# Revit family: Genelec_4410
name_source: partatom
category: Generic Models
units: mm (PartAtom-declared; Revit-internal decimal feet)

## family parameters
Always vertical = No
Can host rebar = No
Cut with Voids When Loaded = No
Maintain Annotation Orientation = No
Part Type = Normal
Room Calculation Point = Yes
Round Connector Dimension = Use Diameter
Shared = No
Work Plane-Based = No

## types (2) — shared parameters
Accuracy of Frequency Response = ± 2.5 dB (74 Hz - 20 kHz)
Acoustic Axis = 107
BIMobject category = Audio Electronics
Color = RAL_9018_Papyrus White
Connections = 1 x RJ45 for PoE power, management and audio in AES67 / Dante format
Default Elevation = 1200 mm
Depth = 115 mm  [stored 0.377297 ft]
Description = The most compact in the Smart IP family, the 4410A Active PoE-Powered Installation Loudspeaker produces uncompromised SPL and acoustic performance.
Dispersion Angle = H 130° V 110°
Driver Dimensions = ⌀ 76 mm Woofer+ ⌀ 19 mm Tweeter
Export Type to IFC As = IfcAudioVisualApplianceType
Finish Type = Die cast aluminium
Frequency Response = 67 Hz - 40 kHz (-6 dB)
Height = 181 mm  [stored 0.593832 ft]
IFC Classification = Electric Appliance
IFC Name = 4410A
Line Drawing = https://assets.ctfassets.net
Mains Voltage = PoE+/PoE
Manufacturer = GENELEC
Manufacturer Country = Finland
Max. short term sine wave acoustic output  on axis in half space, averaged from 100Hz to 3 kHz = ≥ 96 dB SPL
Maximum long term RMS acoustic output in same conditions with IEC weighted noise (limited by driver unit protection circuit) = ≥ 91 dB SPL
Model = 4410
Model Description = Smart IP Installation Speaker
Model Image = https://images.ctfassets.net
Model Name = 4410A
Mounting Type = Includes mount: 8010-410B/W
Power Consumption = 30 W
Power consumption Idle = ≤4 W
Power consumption Standby = ≤3 W (ISS Active)
Price List Description = Compact aluminium cabinet with tightly controlled directivity and minimum diffraction for excellent clarity and intelligibility. Both drivers have metal protection grilles, with 76 mm (3 in) LF and 19 mm (3/4 in) HF transducers. Integrated crossover and class D amplifiers. Max. SPL 96 dB, frequency response 67 Hz – 40 kHz (-6 dB). Control by Smart IP Manager software, including device discovery, room equalisation, system organization and status monitoring. On-Off switch on the rear panel. Dimensions: H 181 mm x W 121 mm x D 115 mm, weight 1.5 kg.
Product Family = Installation Speaker
Product Group = 4000 Series Installation Speakers
Self-generated Noise = ≤5 dB
Type IFC Predefined Type = SPEAKER
Type Image = <None>
URL = https://www.genelec.com
Uniclass 2.0 Description = Sound Amplifiers
Weight = 1.5
Width = 121 mm  [stored 0.396982 ft]

## per-type parameters (varying)
| type | Horizontal Visibility | Vertical Visibility |
| 4410 Vertical | No | Yes |
| 4410 Horizontal | Yes | No |

note: [stored X ft] marks values corroborated as IEEE doubles in the binary element streams (Revit-internal decimal feet)

## geometry (parser evidence)
native form markers: Sweep x2
no freeform markers — native parametric forms only
